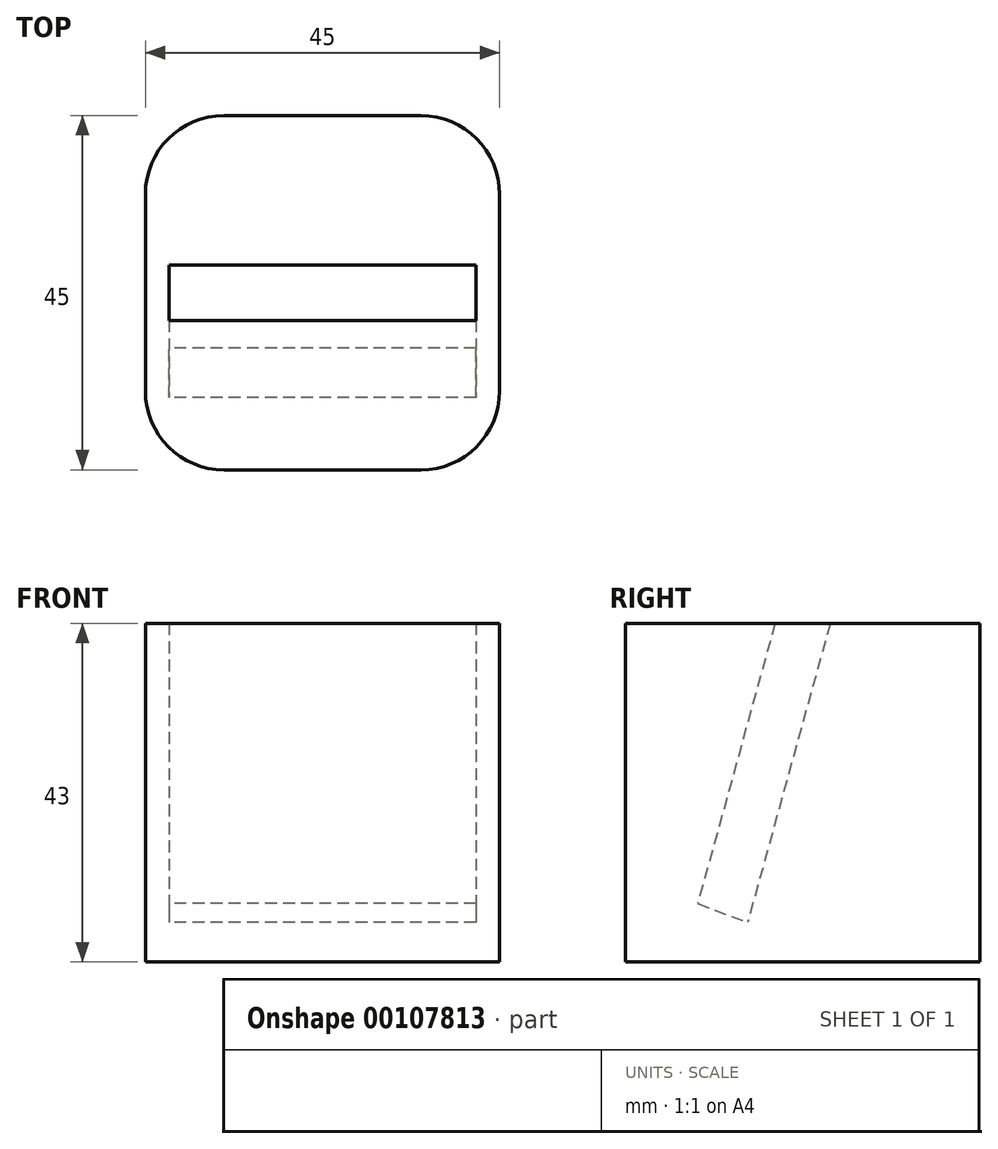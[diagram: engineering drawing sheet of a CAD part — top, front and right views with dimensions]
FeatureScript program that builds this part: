
annotation { "Feature Type Name" : "Feature", "Feature Type Description" : "" }
export const myFeature = defineFeature(function(context is Context, id is Id, definition is map)
    precondition{}
    {
        {
            var Q0;
            Q0=qCreatedBy(makeId("Top.planeOp"),FACE);
            var sketch = newSketch(context, id + "F0", { "sketchPlane" : qUnion([Q0])});
            skLineSegment(sketch, "E0.bottom", {"start": v(12.5, -22.5) * mm, "end": v(-12.5, -22.5) * mm});
            skLineSegment(sketch, "E0.top", {"start": v(12.5, 22.5) * mm, "end": v(-12.5, 22.5) * mm});
            skLineSegment(sketch, "E0.left", {"start": v(22.5, -12.5) * mm, "end": v(22.5, 12.5) * mm});
            skLineSegment(sketch, "E0.right", {"start": v(-22.5, -12.5) * mm, "end": v(-22.5, 12.5) * mm});
            skPoint(sketch, "E0.middle", {"position": v(0, 0) * mm});
            skPoint(sketch, "E1.visualSharp", {"position": v(22.5, 22.5) * mm});
            skArc(sketch, "E1.filletArc", {"start": v(22.5, 12.5) * mm, "mid": v(19.57, 19.57) * mm, "end": v(12.5, 22.5) * mm});
            skPoint(sketch, "E2.visualSharp", {"position": v(-22.5, 22.5) * mm});
            skArc(sketch, "E2.filletArc", {"start": v(-12.5, 22.5) * mm, "mid": v(-19.57, 19.57) * mm, "end": v(-22.5, 12.5) * mm});
            skPoint(sketch, "E3.visualSharp", {"position": v(-22.5, -22.5) * mm});
            skArc(sketch, "E3.filletArc", {"start": v(-22.5, -12.5) * mm, "mid": v(-19.57, -19.57) * mm, "end": v(-12.5, -22.5) * mm});
            skPoint(sketch, "E4.visualSharp", {"position": v(22.5, -22.5) * mm});
            skArc(sketch, "E4.filletArc", {"start": v(12.5, -22.5) * mm, "mid": v(19.57, -19.57) * mm, "end": v(22.5, -12.5) * mm});
            skSolve(sketch);
        }
        {
            var Q0;
            Q0 = qSketchRegion(id + "F0", true);
            extrude(context, id + "F1", {"entities" : qUnion([Q0]), "depth" : 43 * mm});
        }
        {
            var Q0;
            Q0=makeQuery(id+"F1.opExtrude","CAP_FACE",FACE,{"disambiguationData":[OSD([sQuery(id+"F0.wireOp",EDGE,"E0.bottom"),sQuery(id+"F0.wireOp",EDGE,"E0.top"),sQuery(id+"F0.wireOp",EDGE,"E0.left"),sQuery(id+"F0.wireOp",EDGE,"E0.right"),sQuery(id+"F0.wireOp",EDGE,"E1.filletArc"),sQuery(id+"F0.wireOp",EDGE,"E2.filletArc"),sQuery(id+"F0.wireOp",EDGE,"E3.filletArc"),sQuery(id+"F0.wireOp",EDGE,"E4.filletArc")])],"isStart":false});
            var sketch = newSketch(context, id + "F2", { "sketchPlane" : qUnion([Q0])});
            skLineSegment(sketch, "E5.bottom", {"start": v(19.5, -3.5) * mm, "end": v(-19.5, -3.5) * mm});
            skLineSegment(sketch, "E5.top", {"start": v(19.5, 3.5) * mm, "end": v(-19.5, 3.5) * mm});
            skLineSegment(sketch, "E5.left", {"start": v(19.5, -3.5) * mm, "end": v(19.5, 3.5) * mm});
            skLineSegment(sketch, "E5.right", {"start": v(-19.5, -3.5) * mm, "end": v(-19.5, 3.5) * mm});
            skPoint(sketch, "E5.middle", {"position": v(0, 0) * mm});
            skSolve(sketch);
        }
        {
            var Q0;
            Q0=qCreatedBy(makeId("Top.planeOp"),FACE);
            cPlane(context, id + "F3", {"entities" : qUnion([Q0]), "cplaneType" : CPlaneType.OFFSET, "offset" : 5 * mm, "width" : 150 * mm, "height" : 150 * mm});
        }
        {
            var Q0;
            Q0=qCreatedBy(id+"F3.planeOp",FACE);
            var sketch = newSketch(context, id + "F4", { "sketchPlane" : qUnion([Q0])});
            skLineSegment(sketch, "E6.bottom", {"start": v(19.5, -14) * mm, "end": v(-19.5, -14) * mm});
            skLineSegment(sketch, "E6.top", {"start": v(19.5, -7) * mm, "end": v(-19.5, -7) * mm});
            skLineSegment(sketch, "E6.left", {"start": v(19.5, -14) * mm, "end": v(19.5, -7) * mm});
            skLineSegment(sketch, "E6.right", {"start": v(-19.5, -14) * mm, "end": v(-19.5, -7) * mm});
            skPoint(sketch, "E6.middle", {"position": v(0, -10.5) * mm});
            skSolve(sketch);
        }
        {
            var Q1;
            Q1 = qSketchRegion(id + "F2", true);
            var Q2;
            Q2 = qSketchRegion(id + "F4", true);
            loft(context, id + "F5", {"operationType" : NewBodyOperationType.REMOVE, "sheetProfilesArray" : [{ "sheetProfileEntities" : qUnion([Q1]) }, { "sheetProfileEntities" : qUnion([Q2]) }]});
        }
        {
            var Q0;
            Q0=makeQuery(id+"F5.boolean.opBoolean","COPY",FACE,{"derivedFrom":makeQuery(id+"F5.opLoft","CAP_FACE",FACE,{"disambiguationData":[OSD([makeQuery(id+"F4.imprint","IMPRINT",FACE,{"disambiguationData":[TD([[makeQuery(id+"F4.imprint","IMPRINT",EDGE,{"derivedFrom":sQuery(id+"F4.wireOp",EDGE,"E6.bottom")}),-1.0]])]})])],"isStart":true})});
            var sketch = newSketch(context, id + "F6", { "sketchPlane" : qUnion([Q0])});
            skLineSegment(sketch, "E7", {"start": v(-19.5, -7) * mm, "end": v(19.5, -7) * mm});
            skLineSegment(sketch, "E8", {"start": v(19.5, -7) * mm, "end": v(19.5, -14) * mm});
            skLineSegment(sketch, "E9", {"start": v(19.5, -14) * mm, "end": v(-19.5, -14) * mm});
            skLineSegment(sketch, "E10", {"start": v(-19.5, -14) * mm, "end": v(-19.5, -7) * mm});
            skSolve(sketch);
        }
        {
            var Q0;
            Q0 = qSketchRegion(id + "F6", true);
            var Q1;
            Q1=sQuery(id+"F6.wireOp",EDGE,"E7");
            revolve(context, id + "F7", {"operationType" : NewBodyOperationType.ADD, "entities" : qUnion([Q0]), "axis" : qUnion([Q1]), "revolveType" : RevolveType.ONE_DIRECTION, "oppositeDirection" : true, "angle" : 20.8 * degree});
        }
    });
